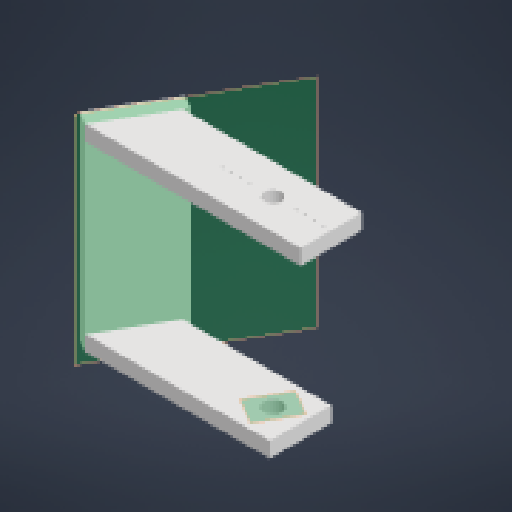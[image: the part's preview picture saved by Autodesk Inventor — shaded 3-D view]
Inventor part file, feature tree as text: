
AUTODESK INVENTOR PART (.ipt)
format: ipt  version: 2024 (Build 280153000, 153)  size: 225,792 bytes
history: native  units: mm
features: other x17, reference x11, extrude x4, sketch x4
ambient origin geometry x8: Origin, YZ Plane, XZ Plane, XY Plane, X Axis, Y Axis, Z Axis, Center Point
bodies: Body1 (feature_tree)
feature tree (36):
  other  "Твердое тело1"
  extrude  "Выдавливание1"  Depth=20.0mm
  other  "РабПлоскость1"
  extrude  "Выдавливание2"  Depth=5.0mm TaperAngle=0.0deg
  other  "РабПлоскость3"
  extrude  "Выдавливание3"  Depth=100.0mm
  other  "Непосредственное редактирование1"
  extrude  "Выдавливание4"  Depth=90.0mm
  sketch  "Эскиз1"
  reference  "Ссылка1"
  sketch  "Эскиз2"
  reference  "Ссылка2"
  other  "РабПлоскость2"
  sketch  "Эскиз3"
  reference  "Ссылка3"
  reference  "Ссылка4"
  reference  "Ссылка5"
  reference  "Ссылка6"
  reference  "Ссылка7"
  reference  "Ссылка8"
  reference  "Ссылка9"
  reference  "Ссылка10"
  reference  "Ссылка11"
  sketch  "Эскиз4"
  parser-record x1  (decoder bookkeeping rows leaked as tree rows — omitted from the tree; the rows remain in map.json)
  other  "manipulator_asembly.iam"
  other  "MG996R SBORKA:1"
  other  "Servo MG996R arm01:1"
  other  "Servo MG996R:1"
  other  "Перенос1"
  other  "Перенос2"
  other  "Перенос3"
  other  "Перенос4"
  other  "Перенос5"
  other  "Перенос6"
  other  "manipulator_holder:1"
note: 1 file-system path scrubbed to <path> (originals preserved in map.json)
